# Revit family: Single Handle Shower Mixer_TOTO_TBG02301
name_source: partatom
category: 衛生器具
revit_build: Autodesk Revit 2018 (Build: 20181011_1500(x64)
units: mm (PartAtom-declared; Revit-internal decimal feet)

## family parameters
OmniClass タイトル = Sanitary, Laundry, and Cleaning Equipment
OmniClass 番号 = 23.45.00.00
パーツ タイプ = 標準
ロード時にボイドで切り取り = いいえ
丸型コネクタ寸法 = 直径を使用
作業面ベース = いいえ
共有 = いいえ
常に垂直 = はい
部屋計算ポイント = いいえ

## types (1)
- Single Handle Shower Mixer_TOTO_TBG02301
    Finish = faucet_material
    Height = 113.7  [stored 0.373031 ft]
    Length = 136.3  [stored 0.447178 ft]
    TOTO AsiaOceania = TBG02301B
    TOTO AsiaOceania URL = http://asia.toto.com
    TOTO China = TBG02301B
    TOTO China URL = http://www.toto.com.cn
    TOTO HongKong = TBG02301B
    TOTO HongKong URL = http://hk.toto.com
    TOTO India = TBG02301B
    TOTO India URL = https://in.toto.com
    TOTO Korea = TBG02301B
    TOTO Korea URL = https://kr.toto.com
    TOTO Thailand = TBG02301T
    TOTO Thailand URL = https://th.toto.com
    Width = 215
    モデル = TBG02301
    製造元 = TOTO Ltd.
    説明 = Single Handle Shower Mixer/单柄双控淋浴水嘴

note: [stored X ft] marks values corroborated as IEEE doubles in the binary element streams (Revit-internal decimal feet)

## geometry (parser evidence)
native form markers: Blend x2, Sweep x1
no freeform markers — native parametric forms only
